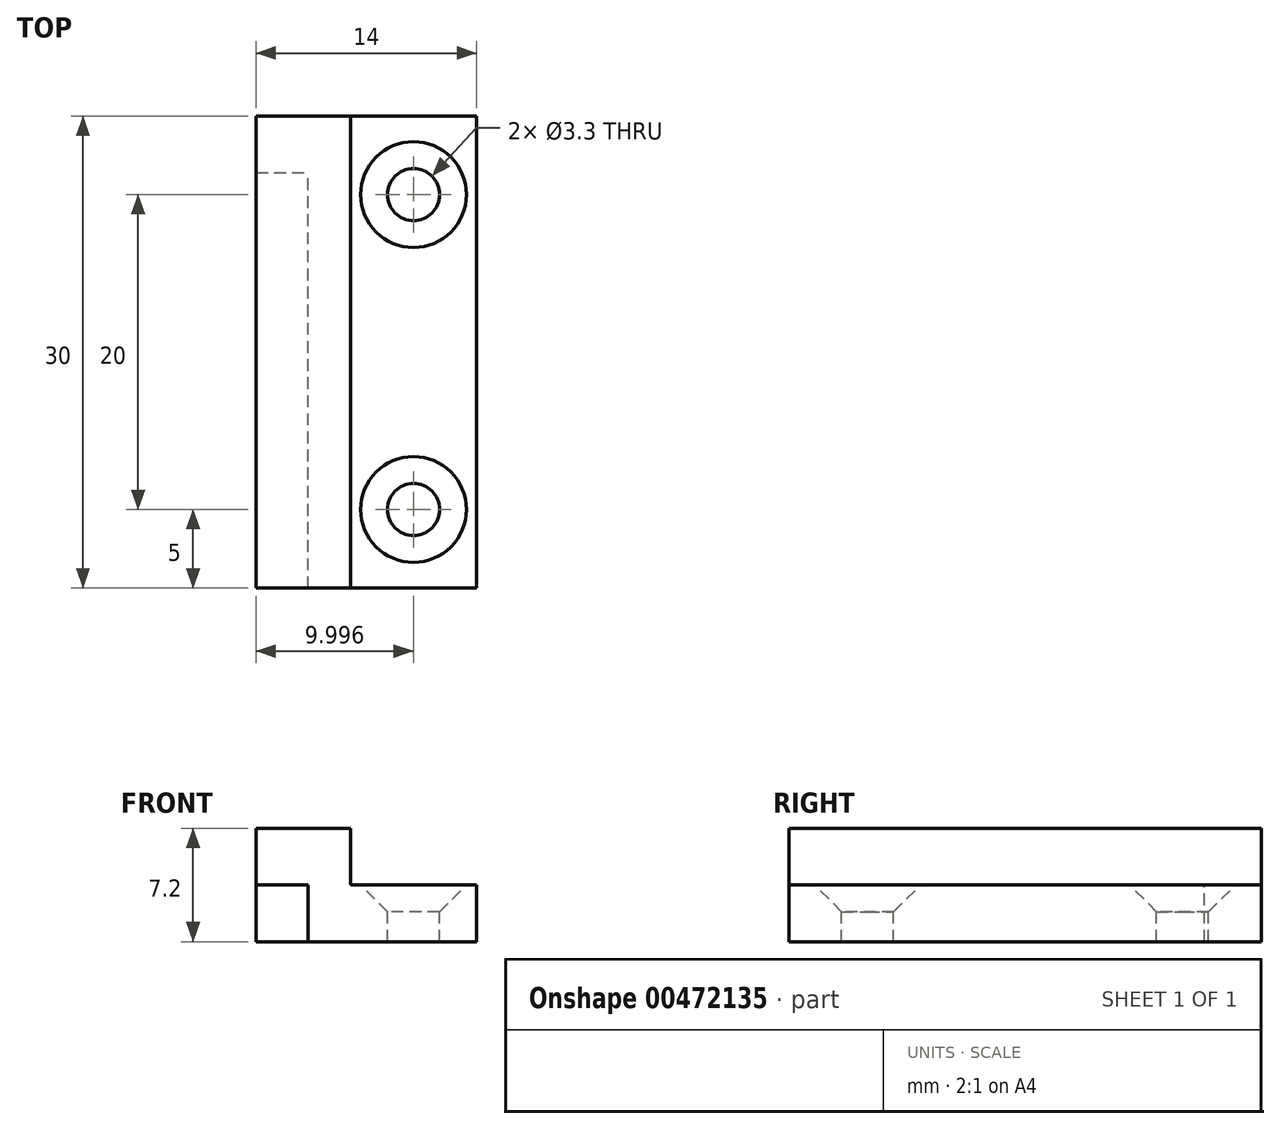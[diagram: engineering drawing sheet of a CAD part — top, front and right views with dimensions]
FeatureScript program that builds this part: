
annotation { "Feature Type Name" : "Feature", "Feature Type Description" : "" }
export const myFeature = defineFeature(function(context is Context, id is Id, definition is map)
    precondition{}
    {
        {
            var Q0;
            Q0=qCreatedBy(makeId("Front.planeOp"),FACE);
            var sketch = newSketch(context, id + "F0", { "sketchPlane" : qUnion([Q0])});
            skLineSegment(sketch, "E0", {"start": v(5.99, 0) * mm, "end": v(-4.71, 0) * mm});
            skLineSegment(sketch, "E1", {"start": v(-4.71, 0) * mm, "end": v(-4.71, 3.6) * mm});
            skLineSegment(sketch, "E2", {"start": v(-4.71, 3.6) * mm, "end": v(-8.01, 3.6) * mm});
            skLineSegment(sketch, "E3", {"start": v(-8.01, 3.6) * mm, "end": v(-8.01, 7.2) * mm});
            skLineSegment(sketch, "E4", {"start": v(-8.01, 7.2) * mm, "end": v(-2.01, 7.2) * mm});
            skLineSegment(sketch, "E5", {"start": v(-2.01, 7.2) * mm, "end": v(-2.01, 3.6) * mm});
            skLineSegment(sketch, "E6", {"start": v(-2.01, 3.6) * mm, "end": v(5.99, 3.6) * mm});
            skLineSegment(sketch, "E7", {"start": v(5.99, 3.6) * mm, "end": v(5.99, 0) * mm});
            skSolve(sketch);
        }
        {
            var Q0;
            Q0=makeQuery(id+"F0.imprint","IMPRINT",FACE,{"disambiguationData":[TD([[makeQuery(id+"F0.imprint","IMPRINT",EDGE,{"derivedFrom":sQuery(id+"F0.wireOp",EDGE,"E0")}),-1.0]])]});
            extrude(context, id + "F1", {"entities" : qUnion([Q0]), "depth" : 30 * mm});
        }
        {
            var Q0;
            Q0=makeQuery(id+"F1.opExtrude","SWEPT_FACE",FACE,{"disambiguationData":[OSD([sQuery(id+"F0.wireOp",EDGE,"E6")])]});
            var sketch = newSketch(context, id + "F2", { "sketchPlane" : qUnion([Q0])});
            skLineSegment(sketch, "E8", {"start": v(1.99, 0) * mm, "end": v(1.99, -30) * mm, "construction": true});
            skPoint(sketch, "E9", {"position": v(1.99, -5) * mm});
            skPoint(sketch, "E10", {"position": v(1.99, -25) * mm});
            skSolve(sketch);
        }
        {
            var Q0;
            Q0=sQuery(id+"F2.wireOp",VERTEX,"E9");
            var Q1;
            Q1=sQuery(id+"F2.wireOp",VERTEX,"E10");
            var Q2;
            Q2=makeQuery(id+"F1.opExtrude","SWEPT_BODY",BODY,{"disambiguationData":[OSD([sQuery(id+"F0.wireOp",EDGE,"E0"),sQuery(id+"F0.wireOp",EDGE,"E1"),sQuery(id+"F0.wireOp",EDGE,"E2"),sQuery(id+"F0.wireOp",EDGE,"E3"),sQuery(id+"F0.wireOp",EDGE,"E4"),sQuery(id+"F0.wireOp",EDGE,"E5"),sQuery(id+"F0.wireOp",EDGE,"E6"),sQuery(id+"F0.wireOp",EDGE,"E7")])]});
            hole(context, id + "F3", {"style" : HoleStyle.C_SINK, "endStyle" : HoleEndStyle.THROUGH, "standardTappedOrClearance" : lookupTablePath({ "standard" : "ISO", "fit" : "Normal", "size" : "M3", "type" : "Clearance" }), "standardBlindInLast" : lookupTablePath({ "fit" : "Standard", "standard" : "ISO", "size" : "M3", "type" : "Clearance" }), "holeDiameter" : 3.3 * mm, "cSinkDiameter" : 6.72 * mm, "cSinkAngle" : 90 * degree, "isTappedThrough" : true, "tappedDepth" : 12 * mm, "tapClearance" : 3, "locations" : qUnion([Q0, Q1]), "scope" : qUnion([Q2])});
        }
        {
            var Q0;
            Q0=makeQuery(id+"F1.opExtrude","SWEPT_FACE",FACE,{"disambiguationData":[OSD([sQuery(id+"F0.wireOp",EDGE,"E1")])]});
            var sketch = newSketch(context, id + "F4", { "sketchPlane" : qUnion([Q0])});
            skLineSegment(sketch, "E11.bottom", {"start": v(0, 0) * mm, "end": v(3.6, 0) * mm});
            skLineSegment(sketch, "E11.top", {"start": v(0, 3.6) * mm, "end": v(3.6, 3.6) * mm});
            skLineSegment(sketch, "E11.left", {"start": v(0, 0) * mm, "end": v(0, 3.6) * mm});
            skLineSegment(sketch, "E11.right", {"start": v(3.6, 0) * mm, "end": v(3.6, 3.6) * mm});
            skSolve(sketch);
        }
        {
            var Q0;
            Q0 = qSketchRegion(id + "F4", true);
            var Q1;
            Q1=makeQuery(id+"F1.opExtrude","CAP_VERTEX",VERTEX,{"disambiguationData":[OSD([sQuery(id+"F0.wireOp",EDGE,"E2"),sQuery(id+"F0.wireOp",EDGE,"E3")])],"isStart":true});
            extrude(context, id + "F5", {"entities" : qUnion([Q0]), "operationType" : NewBodyOperationType.ADD, "endBound" : BoundingType.UP_TO_VERTEX, "endBoundEntityVertex" : qUnion([Q1]), "depth" : 25 * mm});
        }
    });
